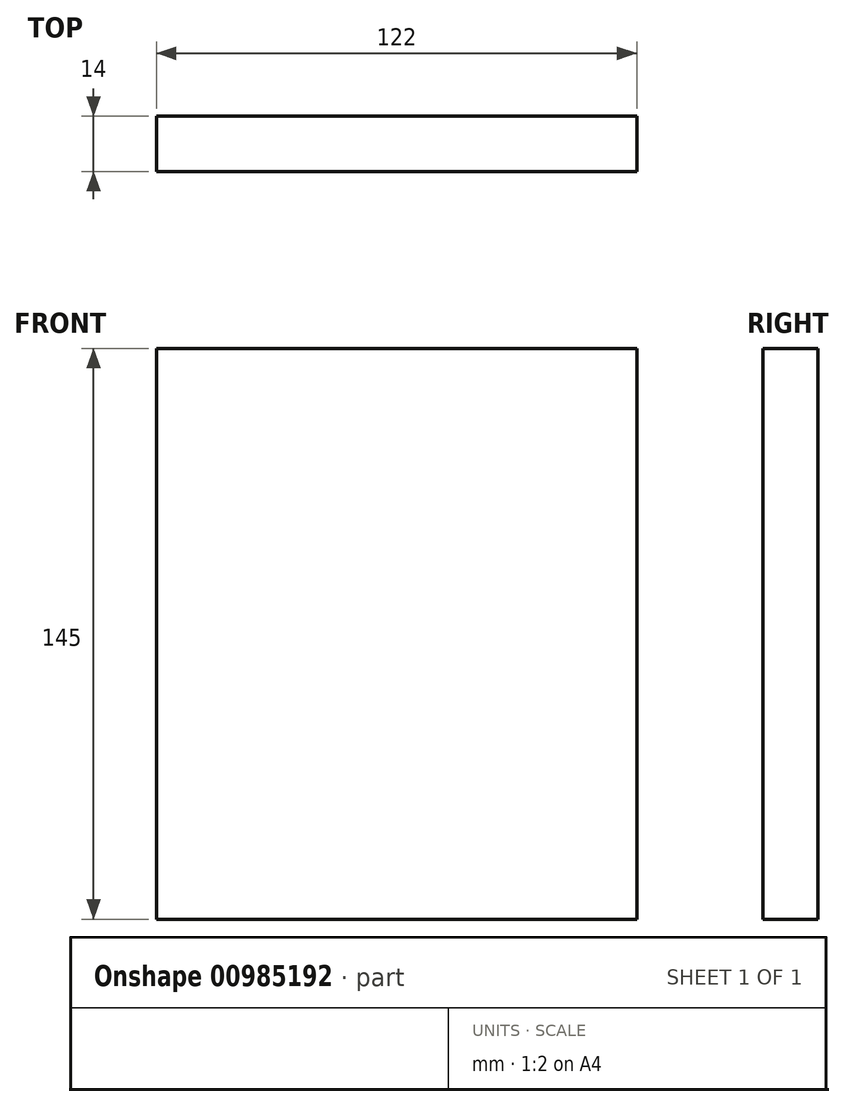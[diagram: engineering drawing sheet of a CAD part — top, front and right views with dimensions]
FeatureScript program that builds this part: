
annotation { "Feature Type Name" : "Feature", "Feature Type Description" : "" }
export const myFeature = defineFeature(function(context is Context, id is Id, definition is map)
    precondition{}
    {
        {
            var Q0;
            Q0=qCreatedBy(makeId("Front.planeOp"),FACE);
            var sketch = newSketch(context, id + "F0", { "sketchPlane" : qUnion([Q0])});
            skLineSegment(sketch, "E0.bottom", {"start": v(-64.23, 71.06) * mm, "end": v(57.77, 71.06) * mm});
            skLineSegment(sketch, "E0.top", {"start": v(-64.23, -73.94) * mm, "end": v(57.77, -73.94) * mm});
            skLineSegment(sketch, "E0.left", {"start": v(-64.23, 71.06) * mm, "end": v(-64.23, -73.94) * mm});
            skLineSegment(sketch, "E0.right", {"start": v(57.77, 71.06) * mm, "end": v(57.77, -73.94) * mm});
            skSolve(sketch);
        }
        {
            var Q0;
            Q0 = qSketchRegion(id + "F0", true);
            extrude(context, id + "F1", {"entities" : qUnion([Q0]), "depth" : 14 * mm, "offsetDistance" : 25 * mm});
        }
    });
